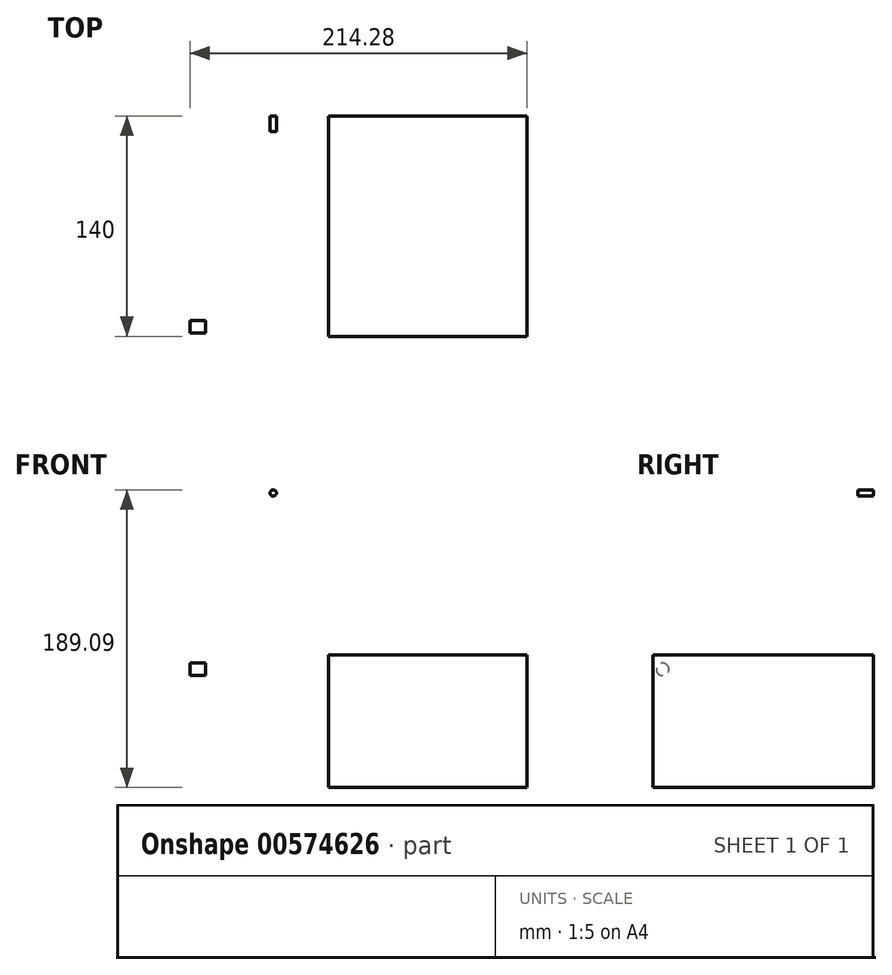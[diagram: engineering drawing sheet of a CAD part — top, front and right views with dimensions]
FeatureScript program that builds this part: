
annotation { "Feature Type Name" : "Feature", "Feature Type Description" : "" }
export const myFeature = defineFeature(function(context is Context, id is Id, definition is map)
    precondition{}
    {
        {
            var Q0;
            Q0=qCreatedBy(makeId("Front.planeOp"),FACE);
            var sketch = newSketch(context, id + "F0", { "sketchPlane" : qUnion([Q0])});
            skCircle(sketch, "E0", {"center": v(0, 0) * mm, "radius": 2 * mm});
            skSolve(sketch);
        }
        {
            var Q0;
            Q0 = qSketchRegion(id + "F0", true);
            extrude(context, id + "F1", {"entities" : qUnion([Q0]), "depth" : 10 * mm, "offsetDistance" : 25 * mm});
        }
        {
            var Q0;
            Q0=qCreatedBy(makeId("Front.planeOp"),FACE);
            var sketch = newSketch(context, id + "F2", { "sketchPlane" : qUnion([Q0])});
            skLineSegment(sketch, "E1.bottom", {"start": v(35, -187.1) * mm, "end": v(161.28, -187.1) * mm});
            skLineSegment(sketch, "E1.top", {"start": v(35, -103) * mm, "end": v(161.28, -103) * mm});
            skLineSegment(sketch, "E1.left", {"start": v(35, -103) * mm, "end": v(35, -187.1) * mm});
            skLineSegment(sketch, "E1.right", {"start": v(161.28, -103) * mm, "end": v(161.28, -187.1) * mm});
            skSolve(sketch);
        }
        {
            var Q0;
            Q0 = qSketchRegion(id + "F2", true);
            extrude(context, id + "F3", {"entities" : qUnion([Q0]), "depth" : 140 * mm, "offsetDistance" : 25 * mm});
        }
        {
            var Q0;
            Q0=qCreatedBy(makeId("Right.planeOp"),FACE);
            cPlane(context, id + "F4", {"entities" : qUnion([Q0]), "cplaneType" : CPlaneType.OFFSET, "offset" : 53 * mm, "oppositeDirection" : true, "width" : 150 * mm, "height" : 150 * mm});
        }
        {
            var Q0;
            Q0=qCreatedBy(id+"F4.planeOp",FACE);
            var sketch = newSketch(context, id + "F5", { "sketchPlane" : qUnion([Q0])});
            skCircle(sketch, "E2", {"center": v(-133.99, -112.02) * mm, "radius": 4 * mm});
            skCircle(sketch, "E3", {"center": v(-81.99, -134.02) * mm, "radius": 4 * mm});
            skCircle(sketch, "E4", {"center": v(-104.99, -51.02) * mm, "radius": 4 * mm});
            skCircle(sketch, "E5", {"center": v(-48.99, -75.02) * mm, "radius": 4 * mm});
            skArc(sketch, "E6", {"start": v(-90.9, -135.29) * mm, "mid": v(-92.29, -131.9) * mm, "end": v(-95.13, -129.58) * mm});
            skArc(sketch, "E7", {"start": v(-90.9, -135.29) * mm, "mid": v(-85.38, -142.35) * mm, "end": v(-76.5, -141.15) * mm});
            skArc(sketch, "E8", {"start": v(-70.41, -139.6) * mm, "mid": v(-73.62, -139.75) * mm, "end": v(-76.5, -141.15) * mm});
            skArc(sketch, "E9", {"start": v(-70.41, -139.6) * mm, "mid": v(-34.54, -122.28) * mm, "end": v(-38.1, -82.61) * mm});
            skArc(sketch, "E10", {"start": v(-40.05, -76.06) * mm, "mid": v(-39.75, -79.54) * mm, "end": v(-38.1, -82.61) * mm});
            skArc(sketch, "E11", {"start": v(-53.71, -67.36) * mm, "mid": v(-44.15, -67.43) * mm, "end": v(-40.05, -76.06) * mm});
            skArc(sketch, "E12", {"start": v(-61.9, -67.84) * mm, "mid": v(-57.75, -68.63) * mm, "end": v(-53.71, -67.36) * mm});
            skLineSegment(sketch, "E13", {"start": v(-91, -54.27) * mm, "end": v(-61.9, -67.84) * mm});
            skArc(sketch, "E14", {"start": v(-96.45, -48.16) * mm, "mid": v(-94.35, -51.78) * mm, "end": v(-91, -54.27) * mm});
            skArc(sketch, "E15", {"start": v(-96.45, -48.16) * mm, "mid": v(-105, -42.02) * mm, "end": v(-113.53, -48.2) * mm});
            skArc(sketch, "E16", {"start": v(-117.09, -53.44) * mm, "mid": v(-114.95, -51.07) * mm, "end": v(-113.53, -48.2) * mm});
            skLineSegment(sketch, "E17", {"start": v(-129.59, -63.93) * mm, "end": v(-117.09, -53.44) * mm});
            skArc(sketch, "E18", {"start": v(-129.59, -63.93) * mm, "mid": v(-135.78, -72) * mm, "end": v(-137.99, -81.95) * mm});
            skLineSegment(sketch, "E19", {"start": v(-137.99, -81.95) * mm, "end": v(-137.99, -98.23) * mm});
            skArc(sketch, "E20", {"start": v(-140.9, -106.25) * mm, "mid": v(-138.74, -102.5) * mm, "end": v(-137.99, -98.23) * mm});
            skArc(sketch, "E21", {"start": v(-140.9, -106.25) * mm, "mid": v(-140, -118.72) * mm, "end": v(-127.5, -118.25) * mm});
            skArc(sketch, "E22", {"start": v(-121.74, -117.17) * mm, "mid": v(-124.79, -116.79) * mm, "end": v(-127.5, -118.25) * mm});
            skLineSegment(sketch, "E23", {"start": v(-121.74, -117.17) * mm, "end": v(-95.13, -129.58) * mm});
            skArc(sketch, "E24", {"start": v(-121.7, -72.98) * mm, "mid": v(-124.86, -77.1) * mm, "end": v(-125.99, -82.17) * mm});
            skLineSegment(sketch, "E25", {"start": v(-121.7, -72.98) * mm, "end": v(-108.5, -61.9) * mm});
            skArc(sketch, "E26", {"start": v(-104.24, -61.34) * mm, "mid": v(-106.45, -61) * mm, "end": v(-108.5, -61.9) * mm});
            skLineSegment(sketch, "E27", {"start": v(-55.27, -84.17) * mm, "end": v(-104.24, -61.34) * mm});
            skArc(sketch, "E28", {"start": v(-74.7, -125.86) * mm, "mid": v(-44.14, -114.74) * mm, "end": v(-55.27, -84.17) * mm});
            skLineSegment(sketch, "E29", {"start": v(-74.7, -125.86) * mm, "end": v(-119.41, -105.02) * mm});
            skArc(sketch, "E30", {"start": v(-125.99, -94.7) * mm, "mid": v(-124.2, -100.81) * mm, "end": v(-119.41, -105.02) * mm});
            skLineSegment(sketch, "E31", {"start": v(-125.99, -82.17) * mm, "end": v(-125.99, -94.7) * mm});
            skSolve(sketch);
        }
        {
            var Q0;
            Q0=makeQuery(id+"F5.imprint","IMPRINT",FACE,{"disambiguationData":[TD([[makeQuery(id+"F5.imprint","IMPRINT",EDGE,{"derivedFrom":sQuery(id+"F5.wireOp",EDGE,"E2")}),1.0]])]});
            extrude(context, id + "F6", {"entities" : qUnion([Q0]), "depth" : 10 * mm, "offsetDistance" : 25 * mm});
        }
    });
